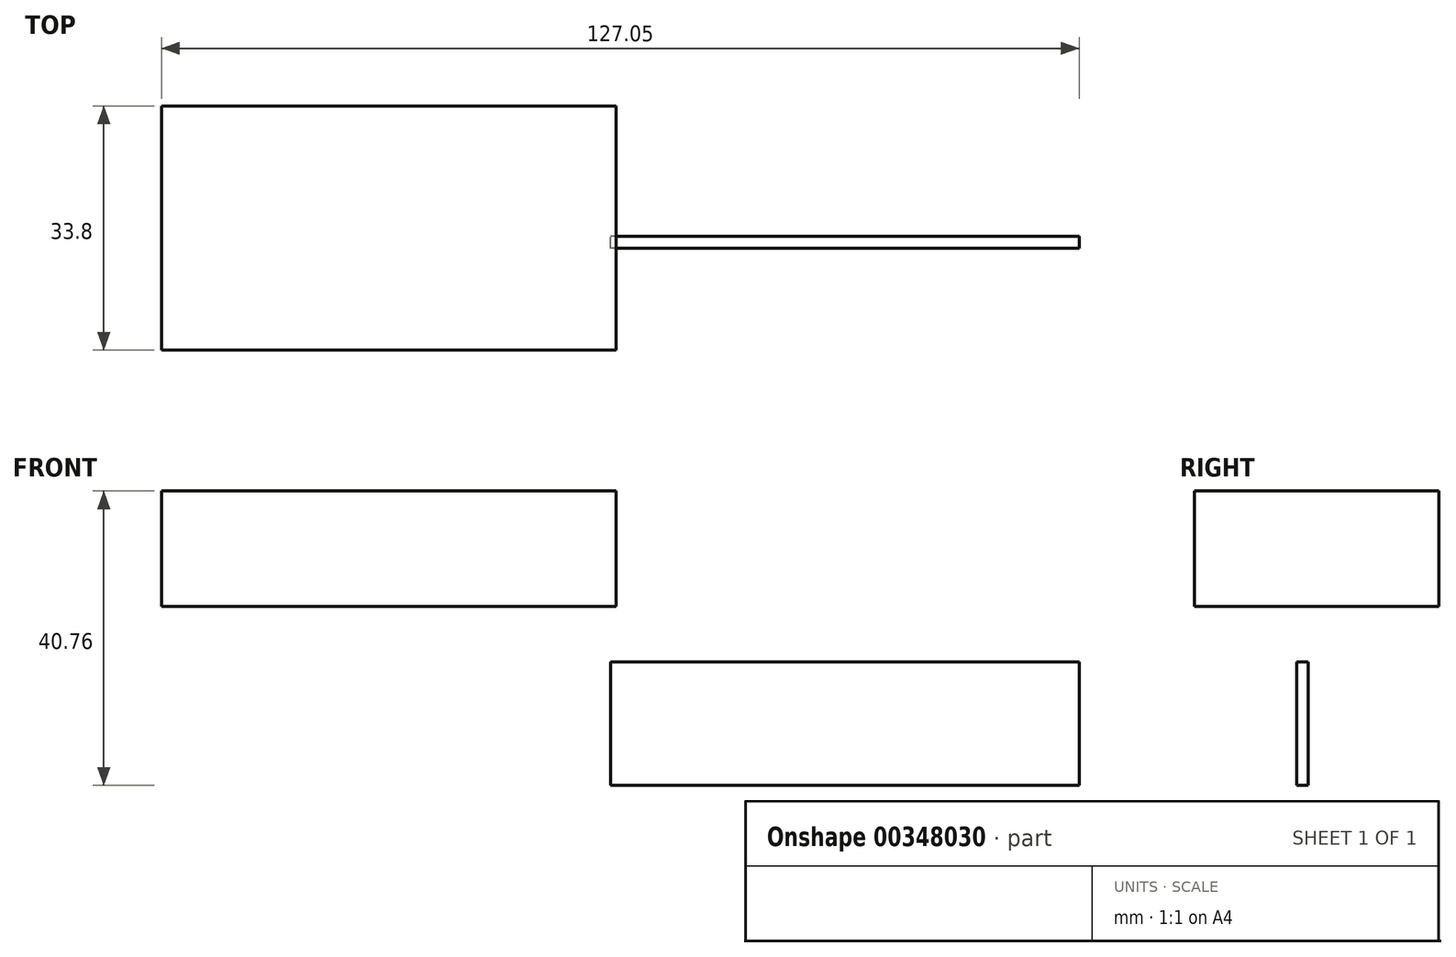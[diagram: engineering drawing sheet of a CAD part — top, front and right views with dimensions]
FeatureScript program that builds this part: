
annotation { "Feature Type Name" : "Feature", "Feature Type Description" : "" }
export const myFeature = defineFeature(function(context is Context, id is Id, definition is map)
    precondition{}
    {
        {
            var Q0;
            Q0=qCreatedBy(makeId("Front.planeOp"),FACE);
            var sketch = newSketch(context, id + "F0", { "sketchPlane" : qUnion([Q0])});
            skLineSegment(sketch, "E0.bottom", {"start": v(95.6, -24.76) * mm, "end": v(30.74, -24.76) * mm});
            skLineSegment(sketch, "E0.top", {"start": v(95.6, -7.68) * mm, "end": v(30.74, -7.68) * mm});
            skLineSegment(sketch, "E0.left", {"start": v(95.6, -24.76) * mm, "end": v(95.6, -7.68) * mm});
            skLineSegment(sketch, "E0.right", {"start": v(30.74, -24.76) * mm, "end": v(30.74, -7.68) * mm});
            skPoint(sketch, "E0.middle", {"position": v(63.17, -16.22) * mm});
            skSolve(sketch);
        }
        {
            var Q0;
            Q0 = qSketchRegion(id + "F0", true);
            extrude(context, id + "F1", {"entities" : qUnion([Q0]), "depth" : 1.6 * mm});
        }
        {
            var Q0;
            Q0=qCreatedBy(makeId("Top.planeOp"),FACE);
            var sketch = newSketch(context, id + "F2", { "sketchPlane" : qUnion([Q0])});
            skLineSegment(sketch, "E1.bottom", {"start": v(31.46, 18.06) * mm, "end": v(-31.46, 18.06) * mm});
            skLineSegment(sketch, "E1.top", {"start": v(31.46, -15.74) * mm, "end": v(-31.46, -15.74) * mm});
            skLineSegment(sketch, "E1.left", {"start": v(31.46, 18.06) * mm, "end": v(31.46, -15.74) * mm});
            skLineSegment(sketch, "E1.right", {"start": v(-31.46, 18.06) * mm, "end": v(-31.46, -15.74) * mm});
            skPoint(sketch, "E1.middle", {"position": v(0, 1.16) * mm});
            skSolve(sketch);
        }
        {
            var Q0;
            Q0 = qSketchRegion(id + "F2", true);
            extrude(context, id + "F3", {"entities" : qUnion([Q0]), "depth" : 16 * mm});
        }
    });
